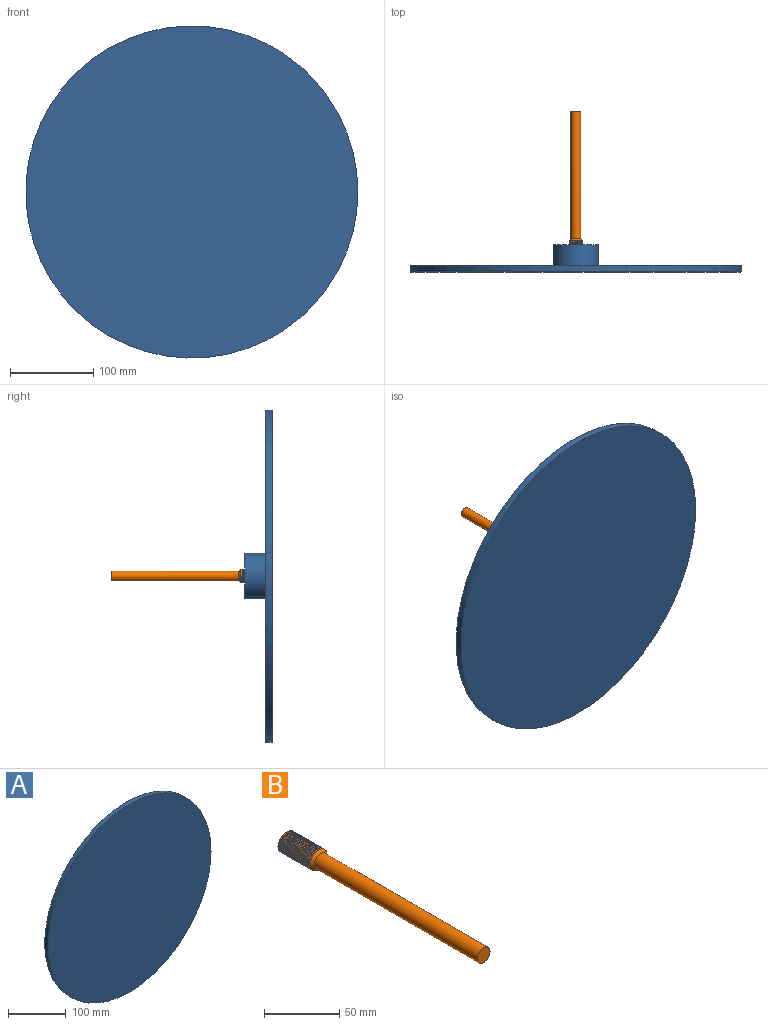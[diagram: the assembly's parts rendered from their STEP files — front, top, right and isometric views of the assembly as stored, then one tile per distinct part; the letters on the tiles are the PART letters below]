
ASSEMBLY  parts=2 mates=1
PART A: 33 faces, bbox 400.1x33.7x400.1 mm
  f0: plane 16.1x16.1mm, normal (0,1,0), area 200.7mm2, adj f24,f27,f28,f29
  f1: cylinder r=200mm len=400mm, axis (0,1,0), area 10053.1mm2, adj f2,f3
  f2: plane 400x400mm, normal (0,-1,0), area 125663.7mm2, adj f1
  f3: plane 400x400mm, normal (0,1,0), area 123287.9mm2, adj f1,f25
  f4: cylinder r=8mm len=16mm, axis (0,-1,0), area 9.9mm2, adj f5,f26,f31
  f5: cylinder r=8mm len=16mm, axis (0,-1,0), area 39.9mm2, adj f4,f6,f26,f31,f32
  f6: cylinder r=8mm len=16mm, axis (0,-1,0), area 40.1mm2, adj f5,f7,f31,f32
  f7: cylinder r=8mm len=16mm, axis (0,-1,0), area 40.1mm2, adj f6,f8,f31,f32
  f8: cylinder r=8mm len=16mm, axis (0,-1,0), area 40.1mm2, adj f7,f9,f31,f32
  f9: cylinder r=8mm len=16mm, axis (0,-1,0), area 40.1mm2, adj f8,f10,f31,f32
  f10: cylinder r=8mm len=16mm, axis (0,-1,0), area 40.1mm2, adj f9,f11,f31,f32
  f11: cylinder r=8mm len=16mm, axis (0,-1,0), area 40.1mm2, adj f10,f12,f31,f32
  f12: cylinder r=8mm len=16mm, axis (0,-1,0), area 40.1mm2, adj f11,f13,f31,f32
  f13: cylinder r=8mm len=16mm, axis (0,-1,0), area 40mm2, adj f12,f14,f31,f32
  f14: cylinder r=8mm len=16mm, axis (0,-1,0), area 40mm2, adj f13,f15,f31,f32
  f15: cylinder r=8mm len=16mm, axis (0,-1,0), area 40.1mm2, adj f14,f16,f31,f32
  f16: cylinder r=8mm len=16mm, axis (0,-1,0), area 40.1mm2, adj f15,f17,f31,f32
  f17: cylinder r=8mm len=16mm, axis (0,-1,0), area 40.1mm2, adj f16,f18,f31,f32
  f18: cylinder r=8mm len=16mm, axis (0,-1,0), area 40.1mm2, adj f17,f19,f31,f32
  f19: cylinder r=8mm len=16mm, axis (0,-1,0), area 40mm2, adj f18,f20,f31,f32
  f20: cylinder r=8mm len=16mm, axis (0,-1,0), area 40.1mm2, adj f19,f21,f31,f32
  f21: cylinder r=8mm len=16mm, axis (0,-1,0), area 40.1mm2, adj f20,f22,f31,f32
  f22: cylinder r=8mm len=16mm, axis (0,-1,0), area 40mm2, adj f21,f23,f31,f32
  f23: cylinder r=8mm len=16mm, axis (0,-1,0), area 40mm2, adj f22,f24,f31,f32
  f24: cylinder r=8mm len=16mm, axis (0,-1,0), area 36.3mm2, adj f0,f23,f30,f32
  f25: cylinder r=27.5mm len=55mm, axis (0,-1,0), area 4319.7mm2, adj f3,f26
  f26: plane 55.13x55.13mm, normal (0,1,0), area 2172mm2, adj f4,f5,f25,f31,f32
  f27: bspline ~7.19x4.44mm, area 0.4mm2, adj f0,f28,f29
  f28: bspline ~6.68x3.86mm, area 0.3mm2, adj f0,f27,f29
  f29: plane 0.16x0.12mm, normal (0,0,-1), area 0mm2, adj f0,f27,f28
  f30: plane 0.45x0.3mm, normal (0,0,-1), area 0.1mm2, adj f24,f31,f32
  f31: bspline ~25.26x19.16mm, area 380.3mm2, adj f4,f5,f6,f7,f8,f9,f10,f11
  f32: bspline ~25.43x19.16mm, area 374.3mm2, adj f5,f6,f7,f8,f9,f10,f11,f12
PART B: 27 faces, bbox 16.4x185.8x18.8 mm
  f0: cylinder r=8mm len=16mm, axis (0,1,0), area 76.3mm2, adj f19,f23,f24,f25,f26
  f1: cylinder r=8mm len=16mm, axis (0,1,0), area 29.1mm2, adj f2,f20,f25,f26
  f2: cylinder r=8mm len=16mm, axis (0,1,0), area 39.4mm2, adj f1,f3,f25,f26
  f3: cylinder r=8mm len=16mm, axis (0,1,0), area 39.4mm2, adj f2,f4,f25,f26
  f4: cylinder r=8mm len=16mm, axis (0,1,0), area 39.4mm2, adj f3,f5,f25,f26
  f5: cylinder r=8mm len=16mm, axis (0,1,0), area 39.4mm2, adj f4,f6,f25,f26
  f6: cylinder r=8mm len=16mm, axis (0,1,0), area 39.4mm2, adj f5,f7,f25,f26
  f7: cylinder r=8mm len=16mm, axis (0,1,0), area 39.4mm2, adj f6,f8,f25,f26
  f8: cylinder r=8mm len=16mm, axis (0,1,0), area 39.4mm2, adj f7,f9,f25,f26
  f9: cylinder r=8mm len=16mm, axis (0,1,0), area 39.4mm2, adj f8,f10,f25,f26
  f10: cylinder r=8mm len=16mm, axis (0,1,0), area 39.4mm2, adj f9,f11,f25,f26
  f11: cylinder r=8mm len=16mm, axis (0,1,0), area 39.4mm2, adj f10,f12,f25,f26
  f12: cylinder r=8mm len=16mm, axis (0,1,0), area 39.4mm2, adj f11,f13,f25,f26
  f13: cylinder r=8mm len=16mm, axis (0,1,0), area 39.4mm2, adj f12,f14,f25,f26
  f14: cylinder r=8mm len=16mm, axis (0,1,0), area 39.4mm2, adj f13,f15,f25,f26
  f15: cylinder r=8mm len=16mm, axis (0,1,0), area 39.4mm2, adj f14,f16,f25,f26
  f16: cylinder r=8mm len=16mm, axis (0,1,0), area 39.4mm2, adj f15,f17,f25,f26
  f17: cylinder r=8mm len=16mm, axis (0,1,0), area 39.4mm2, adj f16,f18,f25,f26
  f18: cylinder r=8mm len=16mm, axis (0,1,0), area 39.4mm2, adj f17,f19,f25,f26
  f19: cylinder r=8mm len=16mm, axis (0,1,0), area 39.4mm2, adj f0,f18,f25,f26
  f20: plane 16.28x15.8mm, normal (0,1,0), area 195.4mm2, adj f1,f25,f26
  f21: cylinder r=6mm len=153mm, axis (0,1,0), area 5768mm2, adj f22,f23
  f22: plane 12x12mm, normal (0,-1,0), area 113.1mm2, adj f21
  f23: cone r=3mm half-angle=45deg, axis (0,1,0), area 124.4mm2, adj f0,f21
  f24: plane 0.72x0.49mm, normal (0,0,1), area 0.2mm2, adj f0,f25,f26
  f25: bspline ~29.66x18.57mm, area 577.9mm2, adj f0,f1,f2,f3,f4,f5,f6,f7
  f26: bspline ~29.37x18.57mm, area 554mm2, adj f0,f1,f2,f3,f4,f5,f6,f7
PLACE A t=(4.22,-11.01,1.56)mm
PLACE B rot(axis=(1,0,0),180deg) t=(4.22,-11.01,1.56)mm
MATE planar B.f0 <-> A.f0  axis (0,-1,0) through (4.22,-11.01,1.56)mm
